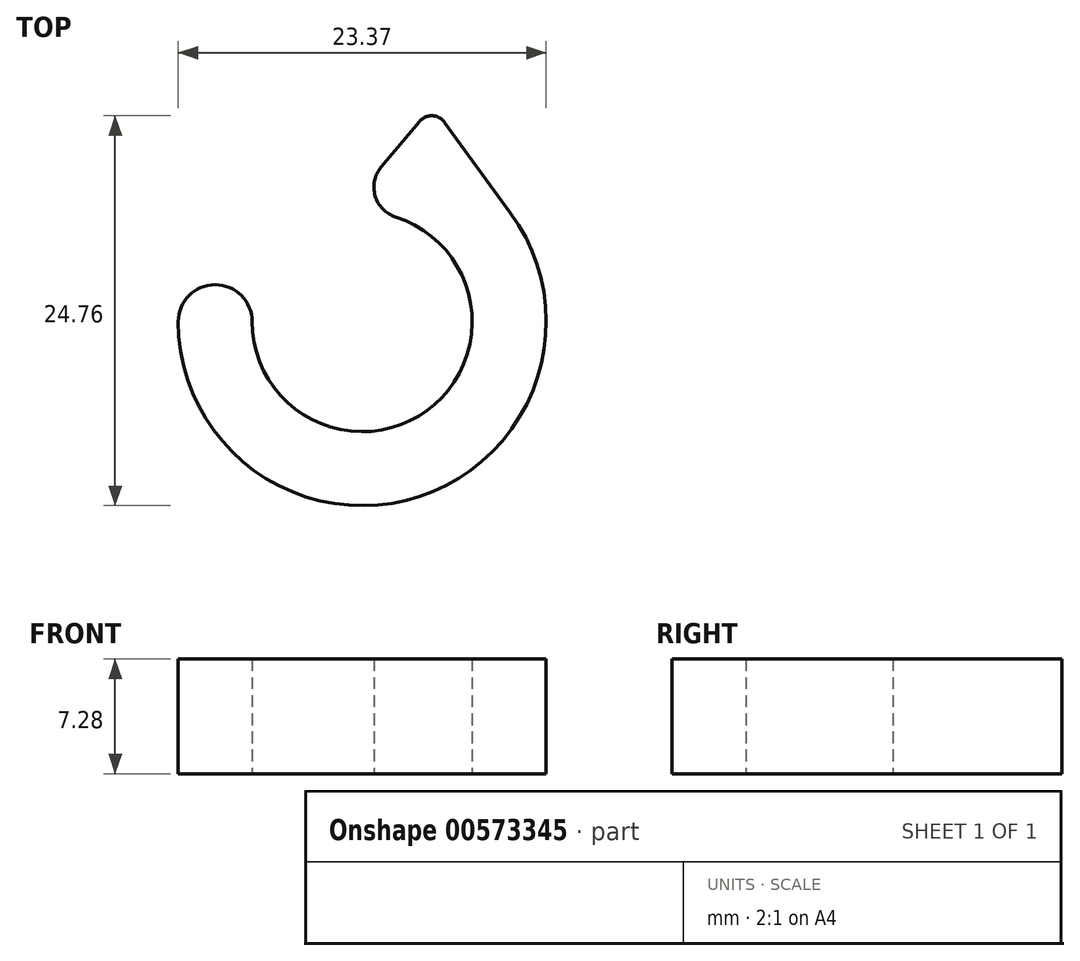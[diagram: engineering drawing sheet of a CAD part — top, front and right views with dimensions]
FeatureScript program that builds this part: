
annotation { "Feature Type Name" : "Feature", "Feature Type Description" : "" }
export const myFeature = defineFeature(function(context is Context, id is Id, definition is map)
    precondition{}
    {
        {
            var Q0;
            Q0=qCreatedBy(makeId("Top.planeOp"),FACE);
            var sketch = newSketch(context, id + "F0", { "sketchPlane" : qUnion([Q0])});
            skPoint(sketch, "E0", {"position": v(-2.35, 0) * mm});
            skLineSegment(sketch, "E1", {"start": v(18.74, 6.94) * mm, "end": v(14.57, 12.66) * mm});
            skLineSegment(sketch, "E2", {"start": v(10.55, 9.83) * mm, "end": v(12.97, 12.72) * mm});
            skArc(sketch, "E3", {"start": v(10.55, 9.83) * mm, "mid": v(10.16, 8) * mm, "end": v(11.46, 6.65) * mm});
            skArc(sketch, "E4", {"start": v(-2.35, 0) * mm, "mid": v(12.99, -11.1) * mm, "end": v(18.74, 6.94) * mm});
            skPoint(sketch, "E5", {"position": v(2.35, 0) * mm});
            skArc(sketch, "E6", {"start": v(2.35, 0) * mm, "mid": v(13.45, -5.64) * mm, "end": v(11.46, 6.65) * mm});
            skArc(sketch, "E7", {"start": v(2.35, 0) * mm, "mid": v(0, 2.35) * mm, "end": v(-2.35, 0) * mm});
            skPoint(sketch, "E8.visualSharp", {"position": v(13.81, 13.72) * mm});
            skArc(sketch, "E8.filletArc", {"start": v(14.57, 12.66) * mm, "mid": v(13.79, 13.08) * mm, "end": v(12.97, 12.72) * mm});
            skSolve(sketch);
        }
        {
            var Q0;
            Q0=makeQuery(id+"F0.imprint","IMPRINT",FACE,{"disambiguationData":[TD([[makeQuery(id+"F0.imprint","IMPRINT",EDGE,{"derivedFrom":sQuery(id+"F0.wireOp",EDGE,"E1")}),1.0]])]});
            extrude(context, id + "F1", {"entities" : qUnion([Q0]), "depth" : 7.28 * mm, "offsetDistance" : 25.4 * mm});
        }
    });
